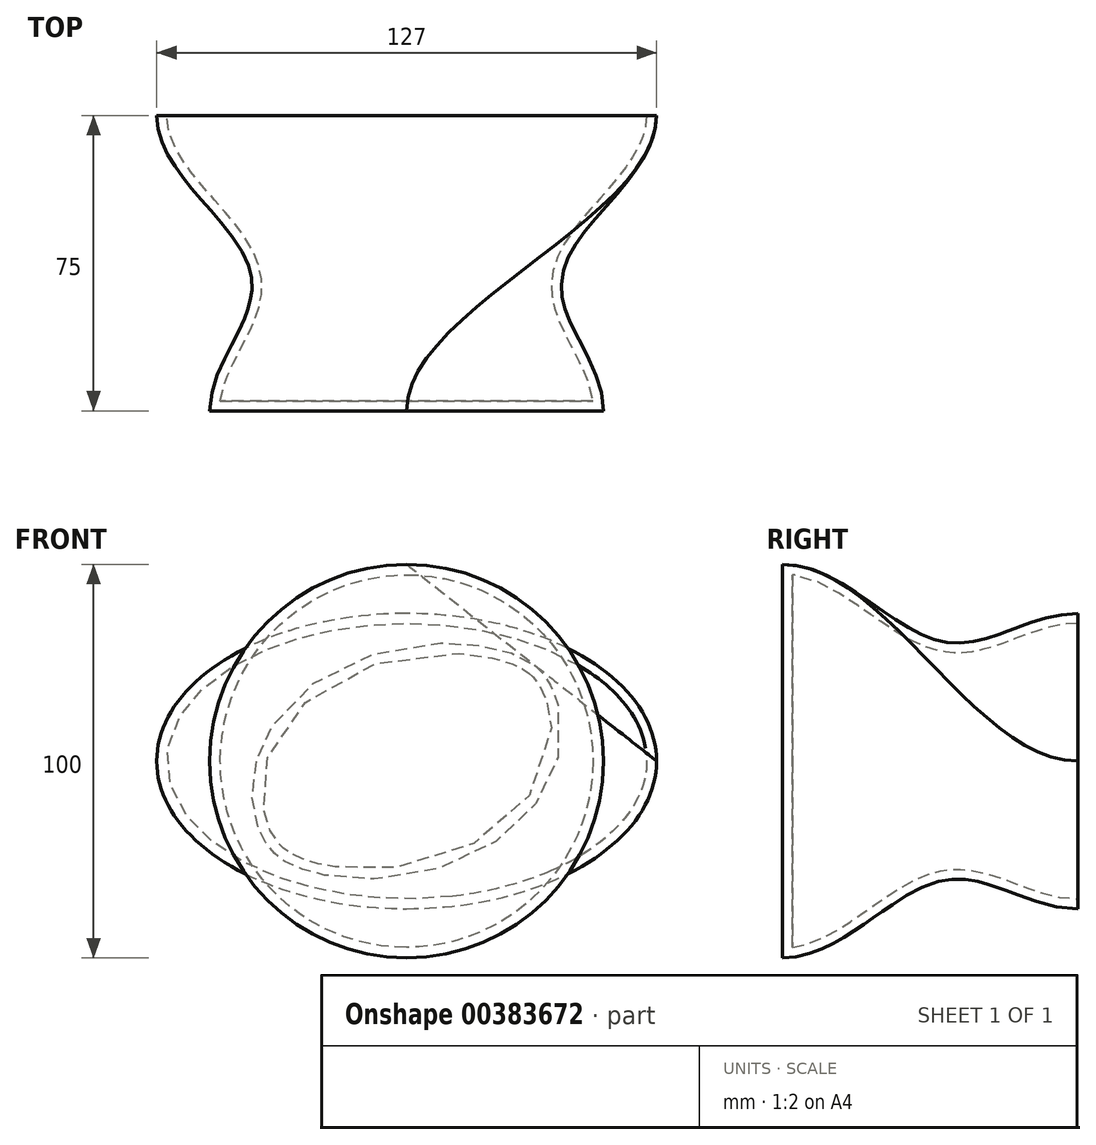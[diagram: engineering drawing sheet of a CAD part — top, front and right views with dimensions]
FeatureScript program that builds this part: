
annotation { "Feature Type Name" : "Feature", "Feature Type Description" : "" }
export const myFeature = defineFeature(function(context is Context, id is Id, definition is map)
    precondition{}
    {
        {
            var Q0;
            Q0=qCreatedBy(makeId("Front.planeOp"),FACE);
            var sketch = newSketch(context, id + "F0", { "sketchPlane" : qUnion([Q0])});
            skArc(sketch, "E0", {"start": v(0, 50) * mm, "mid": v(-35.36, 35.36) * mm, "end": v(-50, 0) * mm});
            skArc(sketch, "E1", {"start": v(50, 0) * mm, "mid": v(35.36, 35.36) * mm, "end": v(0, 50) * mm});
            skArc(sketch, "E2", {"start": v(0, -50) * mm, "mid": v(35.36, -35.36) * mm, "end": v(50, 0) * mm});
            skArc(sketch, "E3", {"start": v(-50, 0) * mm, "mid": v(-35.36, -35.36) * mm, "end": v(0, -50) * mm});
            skSolve(sketch);
        }
        {
            var Q0;
            Q0=makeQuery(id+"F0.imprint","IMPRINT",FACE,{"disambiguationData":[TD([[makeQuery(id+"F0.imprint","IMPRINT",EDGE,{"derivedFrom":sQuery(id+"F0.wireOp",EDGE,"E0")}),1.0]])]});
            cPlane(context, id + "F1", {"entities" : qUnion([Q0]), "cplaneType" : CPlaneType.OFFSET, "offset" : 75 * mm, "oppositeDirection" : true, "width" : 152.4 * mm, "height" : 152.4 * mm});
        }
        {
            var Q0;
            Q0=qCreatedBy(id+"F1.planeOp",FACE);
            var sketch = newSketch(context, id + "F2", { "sketchPlane" : qUnion([Q0])});
            skEllipticalArc(sketch, "E4", {});
            skEllipticalArc(sketch, "E5", {});
            skEllipticalArc(sketch, "E6", {});
            skEllipticalArc(sketch, "E7", {});
            const initialGuessF2  = {"E4": [0, 0, -1, 0, 0.0635, 0.0375, 4.71238898038469, 0], "E5": [0, 0, -1, 0, 0.0635, 0.0375, 0, 1.5707963267948966], "E6": [0, 0, -1, 0, 0.0635, 0.0375, 1.5707963267948966, 3.141592653589793], "E7": [0, 0, -1, 0, 0.0635, 0.0375, 3.141592653589793, 4.71238898038469]};
            skSetInitialGuess(sketch, initialGuessF2);
            skSolve(sketch);
        }
        {
            var Q0;
            Q0 = qSketchRegion(id + "F0", true);
            var Q1;
            Q1 = qSketchRegion(id + "F2", true);
            var Q2;
            Q2=sQuery(id+"F0.wireOp",VERTEX,"E0.start");
            var Q3;
            Q3=sQuery(id+"F2.wireOp",VERTEX,"E7.start");
            loft(context, id + "F3", {"startCondition" : LoftEndDerivativeType.NORMAL_TO_PROFILE, "startMagnitude" : 1, "endCondition" : LoftEndDerivativeType.NORMAL_TO_PROFILE, "endMagnitude" : 1, "sheetProfilesArray" : [{ "sheetProfileEntities" : qUnion([Q0]) }, { "sheetProfileEntities" : qUnion([Q1]) }], "matchConnections" : true, "connections" : [{ "connectionEntities" : qUnion([Q2, Q3]), "connectionEdgeQueries" : qUnion([]), "connectionEdgeParameters" : [] }]});
        }
        {
            var Q0;
            Q0=makeQuery(id+"F3.opLoft","CAP_FACE",FACE,{"disambiguationData":[OSD([makeQuery(id+"F2.imprint","IMPRINT",FACE,{"disambiguationData":[TD([[makeQuery(id+"F2.imprint","IMPRINT",EDGE,{"derivedFrom":sQuery(id+"F2.wireOp",EDGE,"E4")}),1.0]])]})])],"isStart":true});
            shell(context, id + "F4", {"entities" : qUnion([Q0]), "thickness" : 2.5 * mm});
        }
    });
